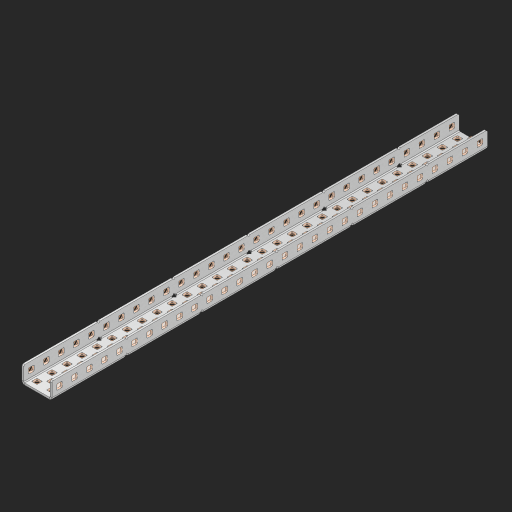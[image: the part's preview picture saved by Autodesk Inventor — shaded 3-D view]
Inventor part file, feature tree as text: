
AUTODESK INVENTOR PART (.ipt)
format: ipt  version: 2023 (Build 270158000, 158)  size: 1,806,336 bytes
history: native  units: in
note: dims shown in document units (in); Inventor stores cm internally (conversion verified against a paired STEP export)
features: other x152, extrude x143, sheet_metal_op x11, sketch x10, pattern_linear x2, mirror x1, chamfer x1
ambient origin geometry x8: Origin, YZ Plane, XZ Plane, XY Plane, X Axis, Y Axis, Z Axis, Center Point
bodies: Solid1 (feature_tree), Body (feature_tree)
feature tree (320):
  sheet_metal_op  "Flanges"
  other  "Flange Pattern Plane"
  other  "Flange Pattern Sketch"
  sheet_metal_op  "Flange Pattern"
  sheet_metal_op  "Body Pattern"
  pattern_linear  "Center Pattern"  Spacing1=0.0625in  [1 undecoded]
  other  "Arc Length"
  mirror  "Notch Mirror"
  pattern_linear  "Notch Pattern"  Spacing1=0.182in  [1 undecoded]
  chamfer  "End Chamfer"
  extrude  "Half Cut"  Depth=0.02in
  sketch  "Sketch1"  dims[d0=1.0in]
  other  "Plate1"
  sketch  "Sketch2"  dims[d1=14.5in]
  other  "Plate2"
  sheet_metal_op  "Bend1"
  sheet_metal_op  "Corner1"
  sketch  "Sketch3"  dims[d2=0.0625in]
  sketch  "Sketch7"  dims[d3=0.0625in]
  other  "Srf1"
  other  "Srf2"
  sketch  "Sketch8"  dims[d4=0.0312in]
  sketch  "Sketch9"  dims[d5=0.125in]
  other  "Srf91"
  sheet_metal_op  "Body Pattern Sketch"
  other  "Srf92"
  sketch  "Sketch13"  dims[d6=0.0625in]
  sketch  "Sketch14"  dims[d7=0.5in d8=90.0deg d9=0.0312in]
  sketch  "Sketch15"  dims[d10=0.25in]
  sketch  "Sketch16"  dims[d11=0.0625in d12=0.0625in d16=0.182in d17=0.02in d18=0.0625in d19=0.0in d20=0.25in d21=0.25in d38=11.4173in d40=0.5in d41=0.7874in d43=1.0in d46=0.172in d47=1.0in d48=0.0in d49=0.182in d50=0.02in d51=0.25in d52=0.25in d53=0.0625in d54=0.0in d55=0.172in d56=1.0in d57=0.0in d58=0.25in d60=11.4173in d62=0.5in d63=0.7874in d65=0.5in d85=0.1473in d86=0.1782in d88=0.04in d89=0.0625in d90=0.0in d91=0.04in d92=0.0491in d95=2.5in d96=0.04in d97=0.25in d98=45.0deg d99=0.25in d100=0.5in d101=0.0in d102=2.497in d106=0.182in d107=0.02in d108=0.5in d109=0.5in d110=0.0625in d111=0.0in d112=0.172in d113=0.5in d114=0.0in d117=0.5in d118=0.5in d119=0.5in]
  other  "Srf786"
  other  "Srf823"
  other  "Srf824"
  other  "Srf825"
  other  "Srf826"
  other  "Srf827"
  other  "Srf828"
  other  "Srf829"
  other  "Srf856"
  other  "Srf857"
  other  "Srf858"
  other  "Srf859"
  other  "Srf860"
  other  "Srf861"
  other  "Srf862"
  other  "Srf889"
  other  "Srf890"
  other  "Srf891"
  other  "Srf892"
  other  "Srf893"
  other  "Srf894"
  other  "Srf895"
  other  "Srf896"
  other  "Srf922"
  other  "Srf923"
  other  "Srf924"
  other  "Srf925"
  other  "Srf926"
  other  "Srf959"
  other  "Srf960"
  other  "Srf961"
  other  "Srf962"
  other  "Srf963"
  other  "Srf996"
  other  "Srf997"
  other  "Srf998"
  other  "Srf999"
  other  "Srf1000"
  other  "Srf1143"
  other  "Srf1144"
  other  "Srf1145"
  other  "Srf1146"
  other  "Srf1147"
  other  "Srf1148"
  other  "Srf1149"
  other  "Srf1150"
  other  "Srf1151"
  other  "Srf1152"
  other  "Srf1153"
  other  "Srf1154"
  other  "Srf1155"
  other  "Srf1156"
  other  "Srf1157"
  other  "Srf1158"
  other  "Srf1159"
  other  "Srf1160"
  other  "Srf1161"
  other  "Srf1162"
  other  "Srf1163"
  other  "Srf1164"
  other  "Srf1165"
  other  "Srf1166"
  other  "Srf1167"
  other  "Srf1168"
  other  "Srf1169"
  other  "Srf1170"
  other  "Srf1171"
  other  "Srf1172"
  other  "Srf1173"
  other  "Srf1174"
  other  "Srf1175"
  other  "Srf1176"
  other  "Srf1177"
  other  "Srf1178"
  other  "Srf1179"
  other  "Srf1180"
  other  "Srf1181"
  other  "Srf1182"
  other  "Srf1183"
  other  "Srf1184"
  other  "Srf1185"
  other  "Srf1186"
  other  "Srf1199"
  other  "Srf1200"
  other  "Srf1201"
  other  "Srf1202"
  other  "Srf1203"
  other  "Srf1204"
  other  "Srf1205"
  other  "Srf1206"
  other  "Srf1207"
  other  "Srf1208"
  other  "Srf1209"
  other  "Srf1210"
  other  "Srf1211"
  other  "Srf1212"
  other  "Srf1213"
  other  "Srf1214"
  other  "Srf1215"
  other  "Srf1216"
  other  "Srf1217"
  other  "Srf1218"
  other  "Srf1219"
  other  "Srf1220"
  other  "Srf1221"
  other  "Srf1222"
  other  "Srf1223"
  other  "Srf1224"
  other  "Srf1225"
  other  "Srf1226"
  other  "Srf1227"
  other  "Srf1228"
  other  "Srf1229"
  other  "Srf1230"
  other  "Srf1231"
  other  "Srf1232"
  other  "Srf1233"
  other  "Srf1234"
  other  "Srf1235"
  other  "Srf1236"
  other  "Srf1237"
  other  "Srf1238"
  other  "Srf1239"
  other  "Srf1240"
  other  "Srf1241"
  other  "Srf1242"
  other  "Srf1255"
  other  "Srf1256"
  other  "Srf1257"
  other  "Srf1258"
  other  "Srf1259"
  other  "Srf1260"
  other  "Srf1261"
  other  "Srf1262"
  other  "Srf1263"
  other  "Srf1264"
  other  "Srf1265"
  other  "Srf1266"
  other  "Srf1267"
  other  "Srf1268"
  other  "Srf1269"
  sheet_metal_op  "Flange Stamp"
  sheet_metal_op  "Flange Circle"
  sheet_metal_op  "Body Stamp"
  sheet_metal_op  "Body Circle"
  other  "Center Stamp"
  other  "Center Circle"
  sheet_metal_op  "Notch"
  extrude  "ExtrusionSrf2"  Depth=0.0625in
  extrude  "ExtrusionSrf92"  TaperAngle=0.0deg  [1 undecoded]
  extrude  "ExtrusionSrf823"  Depth=0.5in
  extrude  "ExtrusionSrf824"  Depth=0.5in
  extrude  "ExtrusionSrf825"  Depth=0.5in
  extrude  "ExtrusionSrf826"  Depth=0.5in
  extrude  "ExtrusionSrf827"  Depth=1.0in TaperAngle=0.0deg
  extrude  "ExtrusionSrf828"  Depth=0.5in
  extrude  "ExtrusionSrf829"  Depth=0.02in
  extrude  "ExtrusionSrf856"  Depth=0.5in
  extrude  "ExtrusionSrf857"  Depth=0.5in
  extrude  "ExtrusionSrf858"  Depth=0.0625in
  extrude  "ExtrusionSrf859"  TaperAngle=0.0deg  [1 undecoded]
  extrude  "ExtrusionSrf860"  Depth=0.5in
  extrude  "ExtrusionSrf861"  Depth=1.0in TaperAngle=0.0deg
  extrude  "ExtrusionSrf862"  Depth=0.5in
  extrude  "ExtrusionSrf889"  Depth=0.5in
  extrude  "ExtrusionSrf890"  Depth=0.5in
  extrude  "ExtrusionSrf891"  Depth=0.5in
  extrude  "ExtrusionSrf892"  Depth=0.5in
  extrude  "ExtrusionSrf893"  Depth=0.5in
  extrude  "ExtrusionSrf894"  Depth=0.0625in
  extrude  "ExtrusionSrf895"  TaperAngle=0.0deg  [1 undecoded]
  extrude  "ExtrusionSrf896"  Depth=0.5in
  extrude  "ExtrusionSrf922"  Depth=0.5in
  extrude  "ExtrusionSrf923"  Depth=2.5in
  extrude  "ExtrusionSrf924"  Depth=0.5in TaperAngle=45.0deg
  extrude  "ExtrusionSrf925"  Depth=0.5in
  extrude  "ExtrusionSrf926"  Depth=0.5in TaperAngle=0.0deg
  extrude  "ExtrusionSrf959"  Depth=0.5in
  extrude  "ExtrusionSrf960"  Depth=0.5in
  extrude  "ExtrusionSrf961"  Depth=0.02in
  extrude  "ExtrusionSrf962"  Depth=0.5in
  extrude  "ExtrusionSrf963"  Depth=0.5in
  extrude  "ExtrusionSrf996"  Depth=0.0625in
  extrude  "ExtrusionSrf997"  TaperAngle=0.0deg  [1 undecoded]
  extrude  "ExtrusionSrf998"  Depth=0.5in
  extrude  "ExtrusionSrf999"  Depth=0.5in TaperAngle=0.0deg
  extrude  "ExtrusionSrf1000"  Depth=0.5in
  extrude  "ExtrusionSrf1143"  Depth=0.5in
  extrude  "ExtrusionSrf1144"  Depth=0.5in
  extrude  "ExtrusionSrf1145"  [1 undecoded]
  extrude  "ExtrusionSrf1146"  [1 undecoded]
  extrude  "ExtrusionSrf1147"  [1 undecoded]
  extrude  "ExtrusionSrf1148"  [1 undecoded]
  extrude  "ExtrusionSrf1149"  [1 undecoded]
  extrude  "ExtrusionSrf1150"  [1 undecoded]
  extrude  "ExtrusionSrf1151"  [1 undecoded]
  extrude  "ExtrusionSrf1152"  [1 undecoded]
  extrude  "ExtrusionSrf1153"  [1 undecoded]
  extrude  "ExtrusionSrf1154"  [1 undecoded]
  extrude  "ExtrusionSrf1155"  [1 undecoded]
  extrude  "ExtrusionSrf1156"  [1 undecoded]
  extrude  "ExtrusionSrf1157"  [1 undecoded]
  extrude  "ExtrusionSrf1158"  [1 undecoded]
  extrude  "ExtrusionSrf1159"  [1 undecoded]
  extrude  "ExtrusionSrf1160"  [1 undecoded]
  extrude  "ExtrusionSrf1161"  [1 undecoded]
  extrude  "ExtrusionSrf1162"  [1 undecoded]
  extrude  "ExtrusionSrf1163"  [1 undecoded]
  extrude  "ExtrusionSrf1164"  [1 undecoded]
  extrude  "ExtrusionSrf1165"  [1 undecoded]
  extrude  "ExtrusionSrf1166"  [1 undecoded]
  extrude  "ExtrusionSrf1167"  [1 undecoded]
  extrude  "ExtrusionSrf1168"  [1 undecoded]
  extrude  "ExtrusionSrf1169"  [1 undecoded]
  extrude  "ExtrusionSrf1170"  [1 undecoded]
  extrude  "ExtrusionSrf1171"  [1 undecoded]
  extrude  "ExtrusionSrf1172"  [1 undecoded]
  extrude  "ExtrusionSrf1173"  [1 undecoded]
  extrude  "ExtrusionSrf1174"  [1 undecoded]
  extrude  "ExtrusionSrf1175"  [1 undecoded]
  extrude  "ExtrusionSrf1176"  [1 undecoded]
  extrude  "ExtrusionSrf1177"  [1 undecoded]
  extrude  "ExtrusionSrf1178"  [1 undecoded]
  extrude  "ExtrusionSrf1179"  [1 undecoded]
  extrude  "ExtrusionSrf1180"  [1 undecoded]
  extrude  "ExtrusionSrf1181"  [1 undecoded]
  extrude  "ExtrusionSrf1182"  [1 undecoded]
  extrude  "ExtrusionSrf1183"  [1 undecoded]
  extrude  "ExtrusionSrf1184"  [1 undecoded]
  extrude  "ExtrusionSrf1185"  [1 undecoded]
  extrude  "ExtrusionSrf1186"  [1 undecoded]
  extrude  "ExtrusionSrf1199"  [1 undecoded]
  extrude  "ExtrusionSrf1200"  [1 undecoded]
  extrude  "ExtrusionSrf1201"  [1 undecoded]
  extrude  "ExtrusionSrf1202"  [1 undecoded]
  extrude  "ExtrusionSrf1203"  [1 undecoded]
  extrude  "ExtrusionSrf1204"  [1 undecoded]
  extrude  "ExtrusionSrf1205"  [1 undecoded]
  extrude  "ExtrusionSrf1206"  [1 undecoded]
  extrude  "ExtrusionSrf1207"  [1 undecoded]
  extrude  "ExtrusionSrf1208"  [1 undecoded]
  extrude  "ExtrusionSrf1209"  [1 undecoded]
  extrude  "ExtrusionSrf1210"  [1 undecoded]
  extrude  "ExtrusionSrf1211"  [1 undecoded]
  extrude  "ExtrusionSrf1212"  [1 undecoded]
  extrude  "ExtrusionSrf1213"  [1 undecoded]
  extrude  "ExtrusionSrf1214"  [1 undecoded]
  extrude  "ExtrusionSrf1215"  [1 undecoded]
  extrude  "ExtrusionSrf1216"  [1 undecoded]
  extrude  "ExtrusionSrf1217"  [1 undecoded]
  extrude  "ExtrusionSrf1218"  [1 undecoded]
  extrude  "ExtrusionSrf1219"  [1 undecoded]
  extrude  "ExtrusionSrf1220"  [1 undecoded]
  extrude  "ExtrusionSrf1221"  [1 undecoded]
  extrude  "ExtrusionSrf1222"  [1 undecoded]
  extrude  "ExtrusionSrf1223"  [1 undecoded]
  extrude  "ExtrusionSrf1224"  [1 undecoded]
  extrude  "ExtrusionSrf1225"  [1 undecoded]
  extrude  "ExtrusionSrf1226"  [1 undecoded]
  extrude  "ExtrusionSrf1227"  [1 undecoded]
  extrude  "ExtrusionSrf1228"  [1 undecoded]
  extrude  "ExtrusionSrf1229"  [1 undecoded]
  extrude  "ExtrusionSrf1230"  [1 undecoded]
  extrude  "ExtrusionSrf1231"  [1 undecoded]
  extrude  "ExtrusionSrf1232"  [1 undecoded]
  extrude  "ExtrusionSrf1233"  [1 undecoded]
  extrude  "ExtrusionSrf1234"  [1 undecoded]
  extrude  "ExtrusionSrf1235"  [1 undecoded]
  extrude  "ExtrusionSrf1236"  [1 undecoded]
  extrude  "ExtrusionSrf1237"  [1 undecoded]
  extrude  "ExtrusionSrf1238"  [1 undecoded]
  extrude  "ExtrusionSrf1239"  [1 undecoded]
  extrude  "ExtrusionSrf1240"  [1 undecoded]
  extrude  "ExtrusionSrf1241"  [1 undecoded]
  extrude  "ExtrusionSrf1242"  [1 undecoded]
  extrude  "ExtrusionSrf1255"  [1 undecoded]
  extrude  "ExtrusionSrf1256"  [1 undecoded]
  extrude  "ExtrusionSrf1257"  [1 undecoded]
  extrude  "ExtrusionSrf1258"  [1 undecoded]
  extrude  "ExtrusionSrf1259"  [1 undecoded]
  extrude  "ExtrusionSrf1260"  [1 undecoded]
  extrude  "ExtrusionSrf1261"  [1 undecoded]
  extrude  "ExtrusionSrf1262"  [1 undecoded]
  extrude  "ExtrusionSrf1263"  [1 undecoded]
  extrude  "ExtrusionSrf1264"  [1 undecoded]
  extrude  "ExtrusionSrf1265"  [1 undecoded]
  extrude  "ExtrusionSrf1266"  [1 undecoded]
  extrude  "ExtrusionSrf1267"  [1 undecoded]
  extrude  "ExtrusionSrf1268"  [1 undecoded]
  extrude  "ExtrusionSrf1269"  [1 undecoded]
note: 107 required parameter values undecoded (feature->parameter linkage not recoverable at this tier; creation-order binding heuristic only, values carry confidence <= 0.55)
